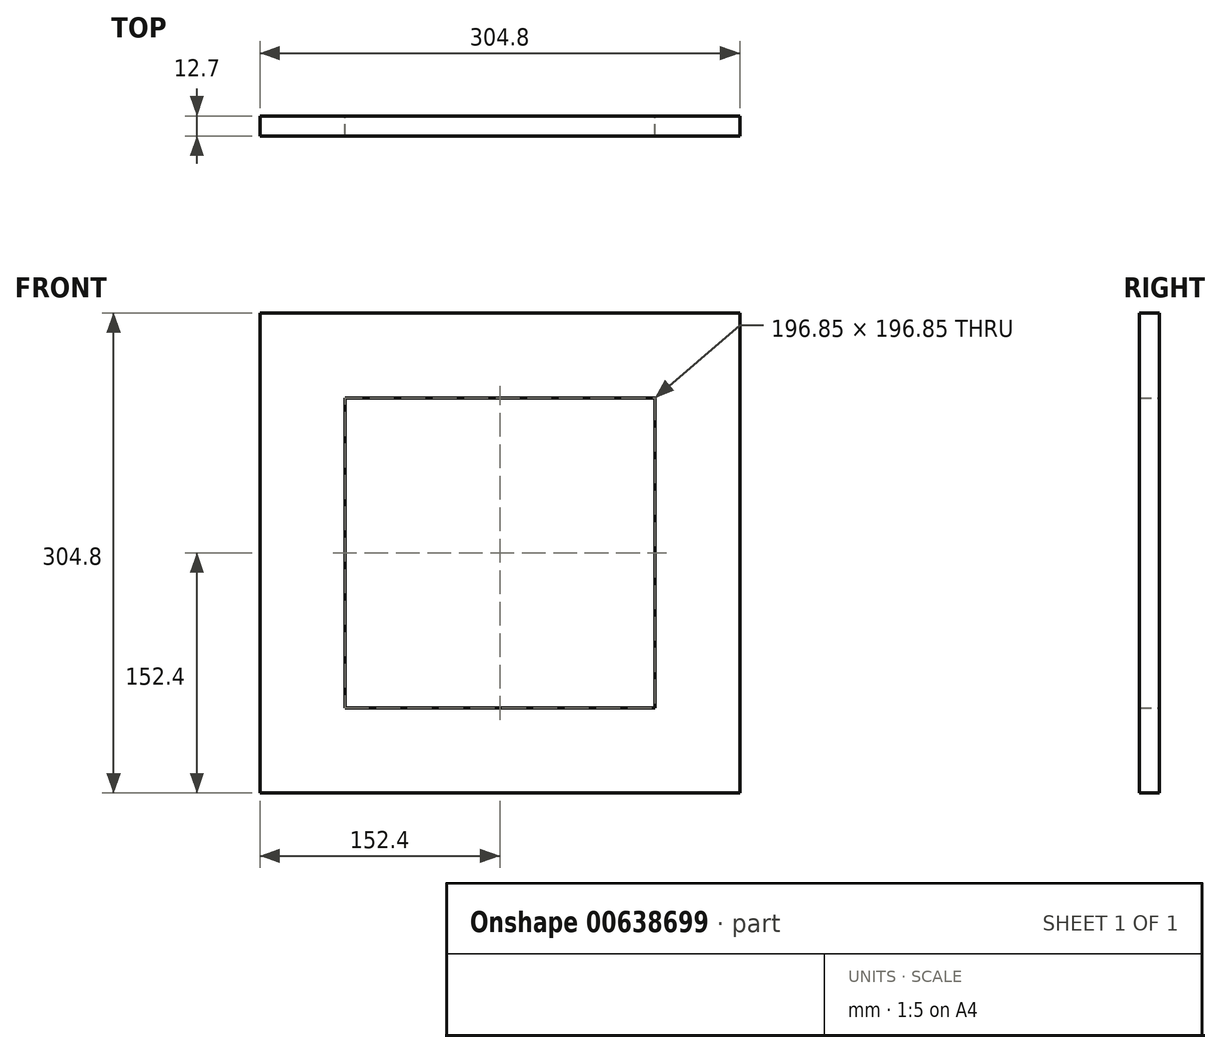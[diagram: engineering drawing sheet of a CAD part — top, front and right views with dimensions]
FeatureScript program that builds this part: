
annotation { "Feature Type Name" : "Feature", "Feature Type Description" : "" }
export const myFeature = defineFeature(function(context is Context, id is Id, definition is map)
    precondition{}
    {
        {
            var Q0;
            Q0=qCreatedBy(makeId("Front.planeOp"),FACE);
            var sketch = newSketch(context, id + "F0", { "sketchPlane" : qUnion([Q0])});
            skLineSegment(sketch, "E0.bottom", {"start": v(0, 0) * mm, "end": v(304.8, 0) * mm});
            skLineSegment(sketch, "E0.top", {"start": v(0, 304.8) * mm, "end": v(304.8, 304.8) * mm});
            skLineSegment(sketch, "E0.left", {"start": v(0, 0) * mm, "end": v(0, 304.8) * mm});
            skLineSegment(sketch, "E0.right", {"start": v(304.8, 0) * mm, "end": v(304.8, 304.8) * mm});
            skLineSegment(sketch, "E1", {"start": v(0, 152.4) * mm, "end": v(152.4, 152.4) * mm, "construction": true});
            skPoint(sketch, "E1.endSnap0", {"position": v(152.4, 304.8) * mm});
            skLineSegment(sketch, "E2.bottom", {"start": v(250.82, 250.83) * mm, "end": v(53.97, 250.83) * mm});
            skLineSegment(sketch, "E2.top", {"start": v(250.82, 53.98) * mm, "end": v(53.97, 53.98) * mm});
            skLineSegment(sketch, "E2.left", {"start": v(250.82, 250.83) * mm, "end": v(250.82, 53.98) * mm});
            skLineSegment(sketch, "E2.right", {"start": v(53.97, 250.83) * mm, "end": v(53.97, 53.97) * mm});
            skPoint(sketch, "E2.middle", {"position": v(152.4, 152.4) * mm});
            skSolve(sketch);
        }
        {
            var Q0;
            Q0 = qSketchRegion(id + "F0", true);
            extrude(context, id + "F1", {"entities" : qUnion([Q0]), "depth" : 12.7 * mm, "offsetDistance" : 25.4 * mm});
        }
    });
